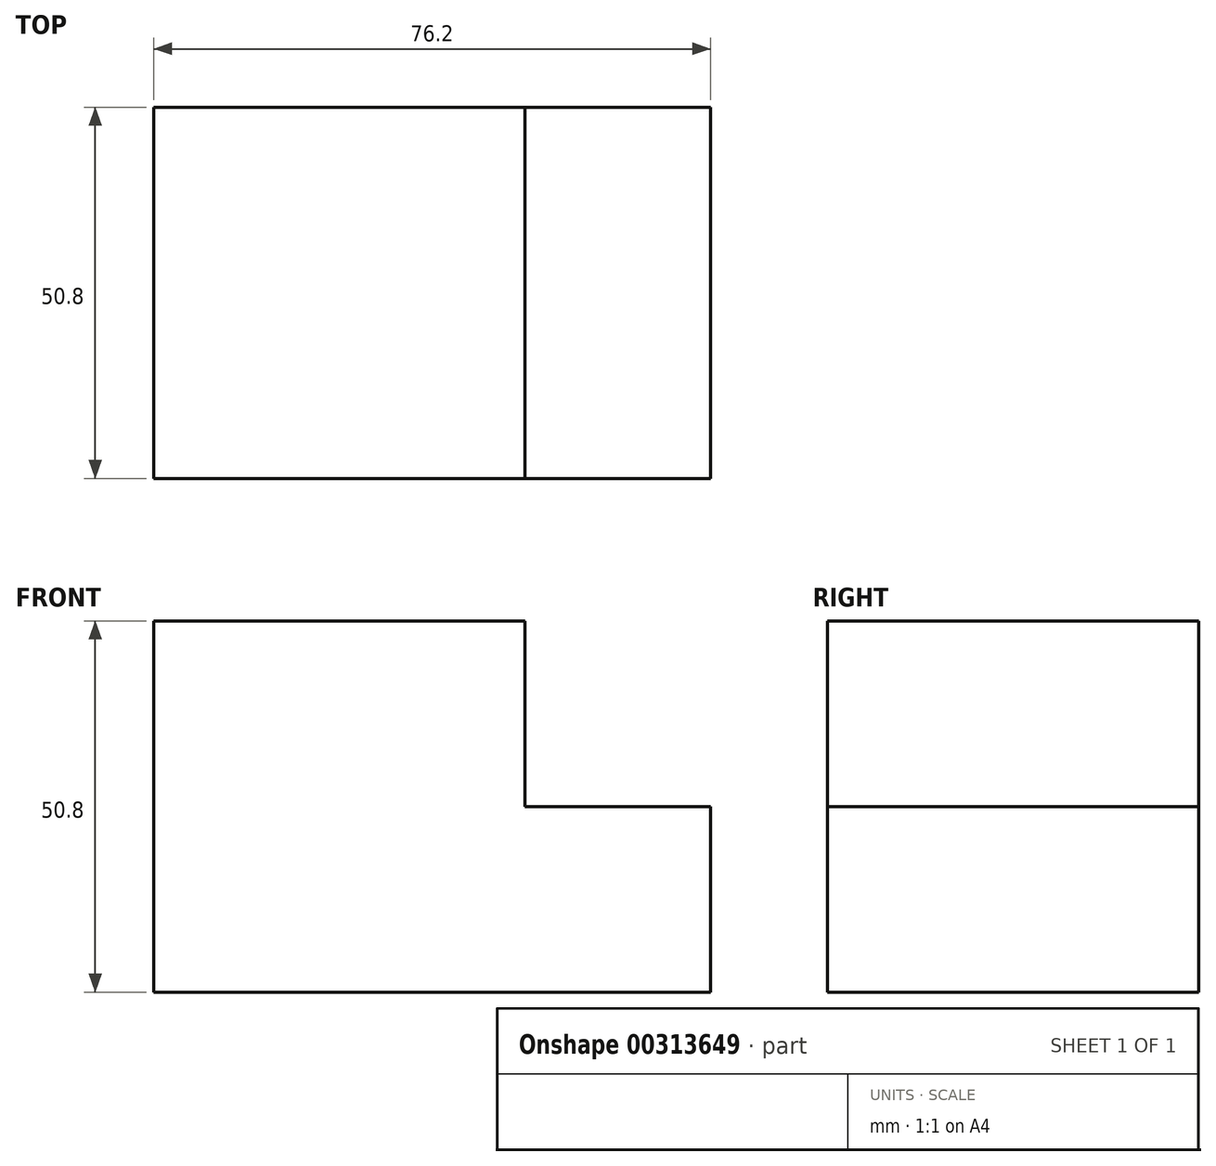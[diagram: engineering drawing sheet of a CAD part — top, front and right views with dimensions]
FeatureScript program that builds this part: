
annotation { "Feature Type Name" : "Feature", "Feature Type Description" : "" }
export const myFeature = defineFeature(function(context is Context, id is Id, definition is map)
    precondition{}
    {
        {
            var Q0;
            Q0=qCreatedBy(makeId("Front.planeOp"),FACE);
            var sketch = newSketch(context, id + "F0", { "sketchPlane" : qUnion([Q0])});
            skLineSegment(sketch, "E0", {"start": v(-31.65, -40.33) * mm, "end": v(44.55, -40.33) * mm});
            skLineSegment(sketch, "E1", {"start": v(44.55, -40.33) * mm, "end": v(44.55, -14.93) * mm});
            skLineSegment(sketch, "E2", {"start": v(44.55, -14.93) * mm, "end": v(19.15, -14.93) * mm});
            skLineSegment(sketch, "E3", {"start": v(19.15, -14.93) * mm, "end": v(19.15, 10.47) * mm});
            skLineSegment(sketch, "E4", {"start": v(19.15, 10.47) * mm, "end": v(-31.65, 10.47) * mm});
            skLineSegment(sketch, "E5", {"start": v(-31.65, 10.47) * mm, "end": v(-31.65, -40.33) * mm});
            skSolve(sketch);
        }
        {
            var Q0;
            Q0 = qSketchRegion(id + "F0", true);
            extrude(context, id + "F1", {"entities" : qUnion([Q0]), "depth" : 25.4 * mm});
        }
        {
            var Q0;
            Q0=makeQuery(id+"F1.opExtrude","CAP_FACE",FACE,{"disambiguationData":[OSD([sQuery(id+"F0.wireOp",EDGE,"E0"),sQuery(id+"F0.wireOp",EDGE,"E1"),sQuery(id+"F0.wireOp",EDGE,"E2"),sQuery(id+"F0.wireOp",EDGE,"E3"),sQuery(id+"F0.wireOp",EDGE,"E4"),sQuery(id+"F0.wireOp",EDGE,"E5")])],"isStart":false});
            extrude(context, id + "F2", {"entities" : qUnion([Q0]), "operationType" : NewBodyOperationType.ADD, "depth" : 25.4 * mm});
        }
    });
